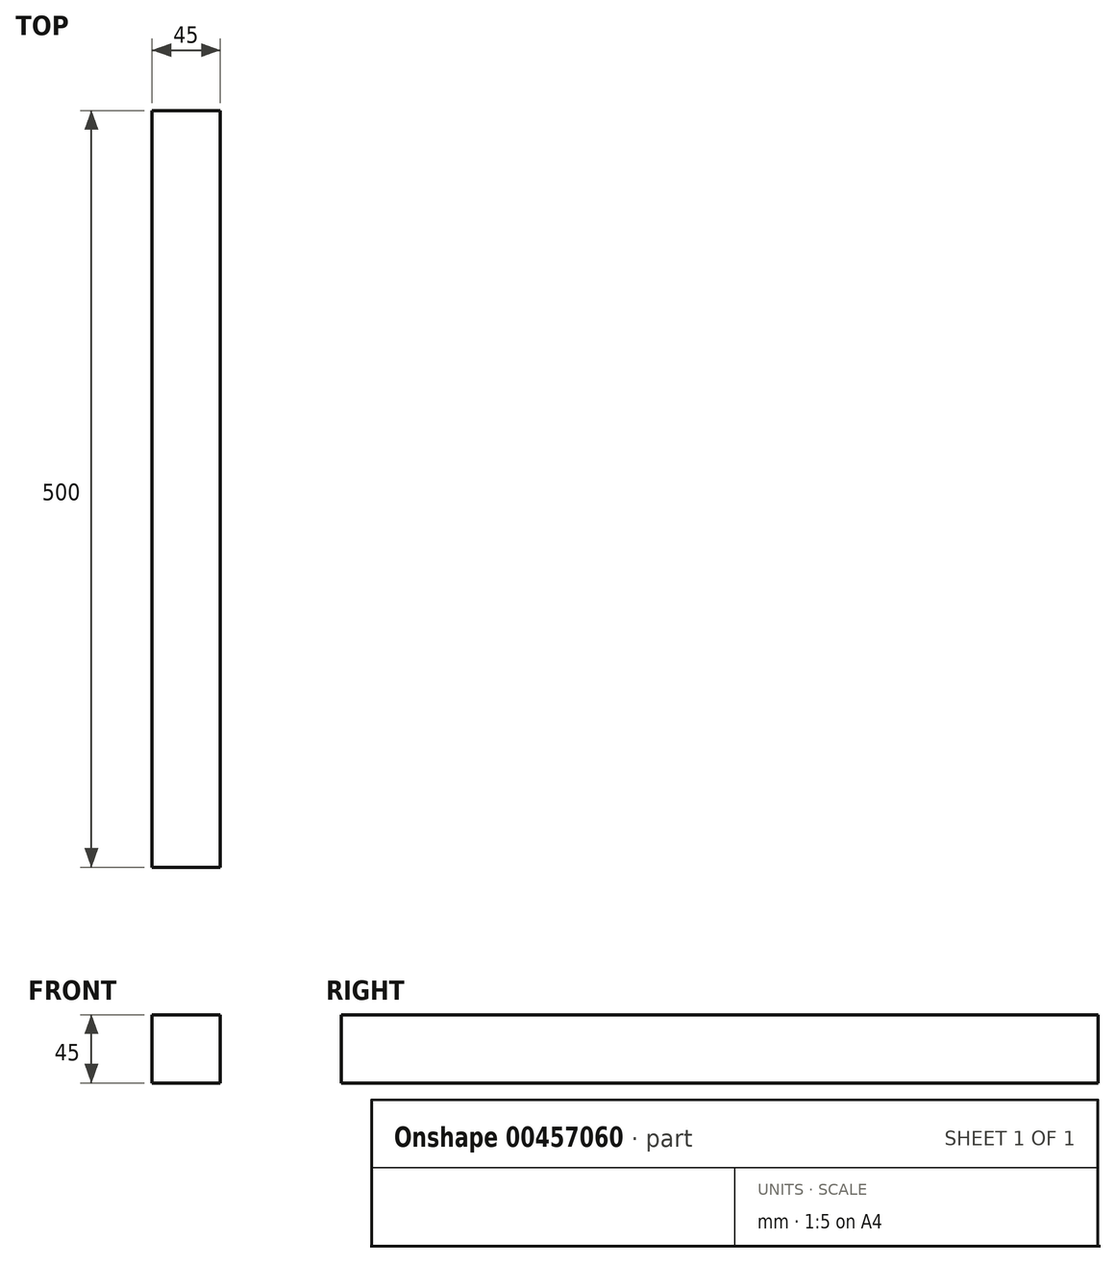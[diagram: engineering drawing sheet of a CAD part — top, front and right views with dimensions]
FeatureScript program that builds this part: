
annotation { "Feature Type Name" : "Feature", "Feature Type Description" : "" }
export const myFeature = defineFeature(function(context is Context, id is Id, definition is map)
    precondition{}
    {
        {
            var Q0;
            Q0=qCreatedBy(makeId("Front.planeOp"),FACE);
            var sketch = newSketch(context, id + "F0", { "sketchPlane" : qUnion([Q0])});
            skLineSegment(sketch, "E0.bottom", {"start": v(22.5, 22.5) * mm, "end": v(-22.5, 22.5) * mm});
            skLineSegment(sketch, "E0.top", {"start": v(22.5, -22.5) * mm, "end": v(-22.5, -22.5) * mm});
            skLineSegment(sketch, "E0.left", {"start": v(22.5, 22.5) * mm, "end": v(22.5, -22.5) * mm});
            skLineSegment(sketch, "E0.right", {"start": v(-22.5, 22.5) * mm, "end": v(-22.5, -22.5) * mm});
            skPoint(sketch, "E0.middle", {"position": v(0, 0) * mm});
            skSolve(sketch);
        }
        {
            var Q0;
            Q0=makeQuery(id+"F0.imprint","IMPRINT",FACE,{"disambiguationData":[TD([[makeQuery(id+"F0.imprint","IMPRINT",EDGE,{"derivedFrom":sQuery(id+"F0.wireOp",EDGE,"E0.bottom")}),1.0]])]});
            extrude(context, id + "F1", {"entities" : qUnion([Q0]), "depth" : 500 * mm});
        }
    });
